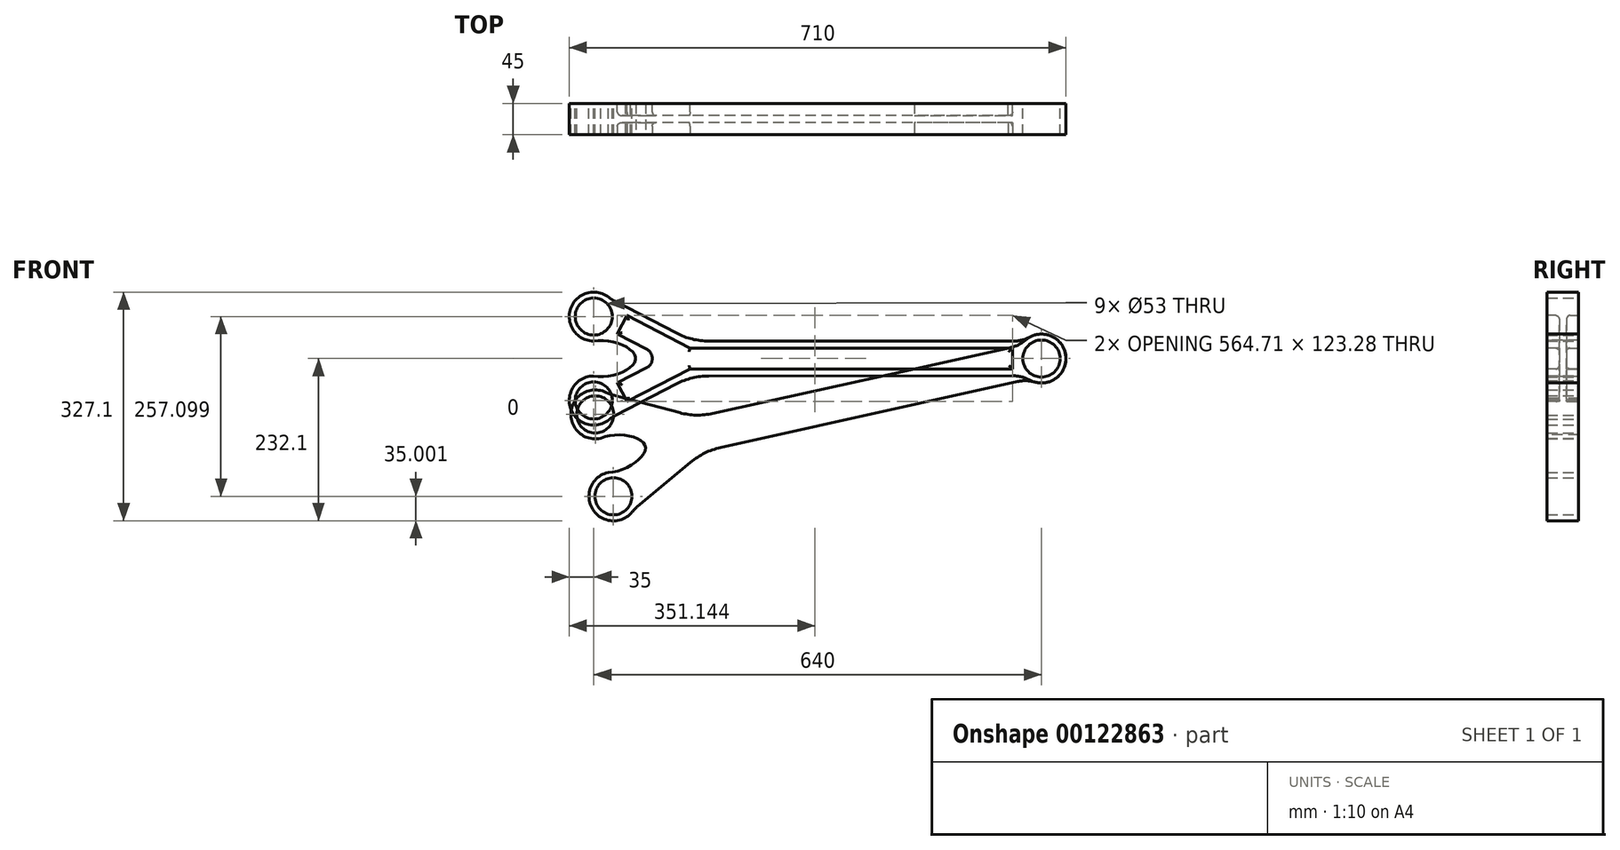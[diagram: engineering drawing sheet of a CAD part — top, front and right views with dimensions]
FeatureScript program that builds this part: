
annotation { "Feature Type Name" : "Feature", "Feature Type Description" : "" }
export const myFeature = defineFeature(function(context is Context, id is Id, definition is map)
    precondition{}
    {
        {
            var Q0;
            Q0=qCreatedBy(makeId("Front.planeOp"),FACE);
            var sketch = newSketch(context, id + "F0", { "sketchPlane" : qUnion([Q0])});
            skArc(sketch, "E0", {"start": v(-16.66, -30.78) * mm, "mid": v(35, 0) * mm, "end": v(-16.66, 30.78) * mm});
            skArc(sketch, "E1", {"start": v(-618.13, 87.33) * mm, "mid": v(-673.03, 71.59) * mm, "end": v(-640, 25) * mm});
            skCircle(sketch, "E2", {"center": v(-700, 0) * mm, "radius": 27.5 * mm, "construction": true});
            skCircle(sketch, "E3", {"center": v(-640, 60) * mm, "radius": 26.5 * mm});
            skCircle(sketch, "E4", {"center": v(-640, -60) * mm, "radius": 26.5 * mm});
            skCircle(sketch, "E5", {"center": v(0, 0) * mm, "radius": 26.5 * mm});
            skLineSegment(sketch, "E6", {"start": v(-40.48, 24.76) * mm, "end": v(-475.65, 24.99) * mm});
            skLineSegment(sketch, "E7", {"start": v(-40.48, -24.76) * mm, "end": v(-475.65, -24.99) * mm});
            skLineSegment(sketch, "E8", {"start": v(-521.62, -36.2) * mm, "end": v(-609.9, -81.98) * mm});
            skLineSegment(sketch, "E9", {"start": v(-521.62, 36.2) * mm, "end": v(-609.9, 81.98) * mm});
            skPoint(sketch, "E10.visualSharp", {"position": v(-500, 25) * mm});
            skArc(sketch, "E10.filletArc", {"start": v(-521.62, 36.2) * mm, "mid": v(-499.3, 27.84) * mm, "end": v(-475.65, 24.99) * mm});
            skPoint(sketch, "E11.visualSharp", {"position": v(-500, -25) * mm});
            skArc(sketch, "E11.filletArc", {"start": v(-475.65, -24.99) * mm, "mid": v(-499.3, -27.84) * mm, "end": v(-521.62, -36.2) * mm});
            skPoint(sketch, "E12.visualSharp", {"position": v(-615.25, 84.75) * mm});
            skArc(sketch, "E13", {"start": v(-640, -25) * mm, "mid": v(-673.03, -71.59) * mm, "end": v(-618.13, -87.33) * mm});
            skFitSpline(sketch, "E14", {"points": [v(-640, -25) * mm, v(-580, 0) * mm, v(-640, 25) * mm], "startDerivative": vector(150, -30) * mm, "endDerivative": vector(-150, -30) * mm});
            skPoint(sketch, "E15.visualSharp", {"position": v(-615.25, -84.75) * mm});
            skLineSegment(sketch, "E16", {"start": v(-24.75, 24.75) * mm, "end": v(0, 0) * mm, "construction": true});
            skLineSegment(sketch, "E17", {"start": v(-24.75, -24.75) * mm, "end": v(0, 0) * mm, "construction": true});
            skPoint(sketch, "E18.visualSharp", {"position": v(-24.75, 24.75) * mm});
            skArc(sketch, "E18.filletArc", {"start": v(-40.48, 24.76) * mm, "mid": v(-28.2, 26.28) * mm, "end": v(-16.66, 30.78) * mm});
            skPoint(sketch, "E19.visualSharp", {"position": v(-24.75, -24.75) * mm});
            skArc(sketch, "E19.filletArc", {"start": v(-16.66, -30.78) * mm, "mid": v(-28.2, -26.28) * mm, "end": v(-40.48, -24.76) * mm});
            skLineSegment(sketch, "E20", {"start": v(-615.25, 84.75) * mm, "end": v(-640, 60) * mm, "construction": true});
            skLineSegment(sketch, "E21", {"start": v(-640, -60) * mm, "end": v(-640, 177.49) * mm, "construction": true});
            skArc(sketch, "E22.filletArc", {"start": v(-618.13, 87.33) * mm, "mid": v(-614.15, 84.45) * mm, "end": v(-609.9, 81.98) * mm});
            skLineSegment(sketch, "E23", {"start": v(-615.25, -84.75) * mm, "end": v(-640, -60) * mm, "construction": true});
            skArc(sketch, "E24.filletArc", {"start": v(-609.9, -81.98) * mm, "mid": v(-614.15, -84.45) * mm, "end": v(-618.13, -87.33) * mm});
            skSolve(sketch);
        }
        {
            var Q0;
            Q0=qSketchRegion(id+"F0",true);
            extrude(context, id + "F1", {"entities" : qUnion([Q0]), "depth" : 45 * mm});
        }
        {
            var Q0;
            Q0=makeQuery(id+"F1.opExtrude","SWEPT_BODY",BODY,{"disambiguationData":[OSD([sQuery(id+"F0.wireOp",EDGE,"E0"),sQuery(id+"F0.wireOp",EDGE,"E1"),sQuery(id+"F0.wireOp",EDGE,"hKVllitM-rUlu-PjKN-B9u5-COeOs3Kio4uB"),sQuery(id+"F0.wireOp",EDGE,"bIEpRebq-8nbQ-7rQF-Jdrm-i3E8cfRsBNN9"),sQuery(id+"F0.wireOp",EDGE,"ymSRshFr-buK2-GFJu-27zL-H9ECYoIg19t0"),sQuery(id+"F0.wireOp",EDGE,"e6450e41-44a2-4cb5-af14-4686bec827bc"),sQuery(id+"F0.wireOp",EDGE,"ipdW7DlG-pZfv-p4Vr-qYAQ-uRQYnpMPVyQN"),sQuery(id+"F0.wireOp",EDGE,"9qNpO7d9-6r7V-397W-DIXA-CVevZtzhY8f4"),sQuery(id+"F0.wireOp",EDGE,"E3"),sQuery(id+"F0.wireOp",EDGE,"E4"),sQuery(id+"F0.wireOp",EDGE,"E5")])]});
            var Q1;
            Q1=makeQuery(id+"F1.opExtrude","CAP_EDGE",EDGE,{"disambiguationData":[OSD([sQuery(id+"F0.wireOp",EDGE,"E5")])],"isStart":false});
            transform(context, id + "F2", {"entities" : qUnion([Q0]), "transformType" : TransformType.ROTATION, "transformAxis" : qUnion([Q1]), "angle" : 12.5 * degree, "makeCopy" : true});
        }
        {
            var Q0;
            Q0=makeQuery(id+"F1.opExtrude","CAP_FACE",FACE,{"disambiguationData":[OSD([sQuery(id+"F0.wireOp",EDGE,"E0"),sQuery(id+"F0.wireOp",EDGE,"E1"),sQuery(id+"F0.wireOp",EDGE,"E3"),sQuery(id+"F0.wireOp",EDGE,"E4"),sQuery(id+"F0.wireOp",EDGE,"E5"),sQuery(id+"F0.wireOp",EDGE,"E6"),sQuery(id+"F0.wireOp",EDGE,"E7"),sQuery(id+"F0.wireOp",EDGE,"E8"),sQuery(id+"F0.wireOp",EDGE,"E9"),sQuery(id+"F0.wireOp",EDGE,"E10.filletArc"),sQuery(id+"F0.wireOp",EDGE,"E11.filletArc"),sQuery(id+"F0.wireOp",EDGE,"E13"),sQuery(id+"F0.wireOp",EDGE,"E14"),sQuery(id+"F0.wireOp",EDGE,"E18.filletArc"),sQuery(id+"F0.wireOp",EDGE,"E19.filletArc"),sQuery(id+"F0.wireOp",EDGE,"E22.filletArc"),sQuery(id+"F0.wireOp",EDGE,"E24.filletArc")])],"isStart":false});
            var sketch = newSketch(context, id + "F3", { "sketchPlane" : qUnion([Q0])});
            skLineSegment(sketch, "E25", {"start": v(-41.5, 14.76) * mm, "end": v(-502.44, 15) * mm});
            skLineSegment(sketch, "E26", {"start": v(-41.5, -14.76) * mm, "end": v(-502.44, -15) * mm});
            skLineSegment(sketch, "E27", {"start": v(-502.44, -15) * mm, "end": v(-592.4, -61.64) * mm});
            skLineSegment(sketch, "E28", {"start": v(-592.4, -61.64) * mm, "end": v(-606.21, -35) * mm});
            skLineSegment(sketch, "E29", {"start": v(-606.21, -35) * mm, "end": v(-564.37, -13.32) * mm});
            skLineSegment(sketch, "E30", {"start": v(-502.44, 15) * mm, "end": v(-592.4, 61.64) * mm});
            skLineSegment(sketch, "E31", {"start": v(-592.4, 61.64) * mm, "end": v(-606.21, 35) * mm});
            skLineSegment(sketch, "E32", {"start": v(-606.21, 35) * mm, "end": v(-564.37, 13.32) * mm});
            skPoint(sketch, "E33.visualSharp", {"position": v(-538.69, 0) * mm});
            skArc(sketch, "E33.filletArc", {"start": v(-564.37, -13.32) * mm, "mid": v(-556.28, 0) * mm, "end": v(-564.37, 13.32) * mm});
            skLineSegment(sketch, "E34", {"start": v(-41.5, 14.76) * mm, "end": v(-41.5, -14.76) * mm});
            skSolve(sketch);
        }
        {
            var Q0;
            Q0=qSketchRegion(id+"F3",true);
            extrude(context, id + "F4", {"entities" : qUnion([Q0]), "operationType" : NewBodyOperationType.REMOVE, "oppositeDirection" : true, "depth" : 17.5 * mm});
        }
        {
            var Q0;
            Q0=makeQuery(id+"F1.opExtrude","CAP_FACE",FACE,{"disambiguationData":[OSD([sQuery(id+"F0.wireOp",EDGE,"E0"),sQuery(id+"F0.wireOp",EDGE,"E1"),sQuery(id+"F0.wireOp",EDGE,"E3"),sQuery(id+"F0.wireOp",EDGE,"E4"),sQuery(id+"F0.wireOp",EDGE,"E5"),sQuery(id+"F0.wireOp",EDGE,"E6"),sQuery(id+"F0.wireOp",EDGE,"E7"),sQuery(id+"F0.wireOp",EDGE,"E8"),sQuery(id+"F0.wireOp",EDGE,"E9"),sQuery(id+"F0.wireOp",EDGE,"E10.filletArc"),sQuery(id+"F0.wireOp",EDGE,"E11.filletArc"),sQuery(id+"F0.wireOp",EDGE,"E13"),sQuery(id+"F0.wireOp",EDGE,"E14"),sQuery(id+"F0.wireOp",EDGE,"E18.filletArc"),sQuery(id+"F0.wireOp",EDGE,"E19.filletArc"),sQuery(id+"F0.wireOp",EDGE,"E22.filletArc"),sQuery(id+"F0.wireOp",EDGE,"E24.filletArc")])],"isStart":true});
            var sketch = newSketch(context, id + "F5", { "sketchPlane" : qUnion([Q0])});
            skLineSegment(sketch, "E35", {"start": v(41.5, 14.76) * mm, "end": v(502.44, 15) * mm});
            skLineSegment(sketch, "E36", {"start": v(502.44, 15) * mm, "end": v(592.4, 61.64) * mm});
            skLineSegment(sketch, "E37", {"start": v(592.4, 61.64) * mm, "end": v(606.21, 35) * mm});
            skLineSegment(sketch, "E38", {"start": v(606.21, -35) * mm, "end": v(592.4, -61.64) * mm});
            skLineSegment(sketch, "E39", {"start": v(592.4, -61.64) * mm, "end": v(502.44, -15) * mm});
            skLineSegment(sketch, "E40", {"start": v(502.44, -15) * mm, "end": v(41.5, -14.76) * mm});
            skLineSegment(sketch, "E41", {"start": v(41.5, 14.76) * mm, "end": v(41.5, -14.76) * mm});
            skLineSegment(sketch, "E42", {"start": v(606.21, 35) * mm, "end": v(564.37, 13.32) * mm});
            skLineSegment(sketch, "E43", {"start": v(564.37, -13.32) * mm, "end": v(606.21, -35) * mm});
            skPoint(sketch, "E44.visualSharp", {"position": v(538.69, 0) * mm});
            skArc(sketch, "E44.filletArc", {"start": v(564.37, 13.32) * mm, "mid": v(556.28, 0) * mm, "end": v(564.37, -13.32) * mm});
            skSolve(sketch);
        }
        {
            var Q0;
            Q0=qSketchRegion(id+"F5",true);
            extrude(context, id + "F6", {"entities" : qUnion([Q0]), "operationType" : NewBodyOperationType.REMOVE, "oppositeDirection" : true, "depth" : 17.5 * mm});
        }
        {
            var Q0;
            Q0=makeQuery(id+"F6.boolean.opBoolean","COPY",EDGE,{"derivedFrom":makeQuery(id+"F6.opExtrude","CAP_EDGE",EDGE,{"disambiguationData":[OSD([sQuery(id+"F5.wireOp",EDGE,"E35")])],"isStart":false})});
            var Q1;
            Q1=makeQuery(id+"F6.boolean.opBoolean","COPY",EDGE,{"derivedFrom":makeQuery(id+"F6.opExtrude","CAP_EDGE",EDGE,{"disambiguationData":[OSD([sQuery(id+"F5.wireOp",EDGE,"E41")])],"isStart":false})});
            var Q2;
            Q2=makeQuery(id+"F6.boolean.opBoolean","COPY",EDGE,{"derivedFrom":makeQuery(id+"F6.opExtrude","CAP_EDGE",EDGE,{"disambiguationData":[OSD([sQuery(id+"F5.wireOp",EDGE,"E40")])],"isStart":false})});
            var Q3;
            Q3=makeQuery(id+"F6.boolean.opBoolean","COPY",EDGE,{"derivedFrom":makeQuery(id+"F6.opExtrude","CAP_EDGE",EDGE,{"disambiguationData":[OSD([sQuery(id+"F5.wireOp",EDGE,"E36")])],"isStart":false})});
            var Q4;
            Q4=makeQuery(id+"F6.boolean.opBoolean","COPY",EDGE,{"derivedFrom":makeQuery(id+"F6.opExtrude","CAP_EDGE",EDGE,{"disambiguationData":[OSD([sQuery(id+"F5.wireOp",EDGE,"E39")])],"isStart":false})});
            var Q5;
            Q5=makeQuery(id+"F6.boolean.opBoolean","COPY",EDGE,{"derivedFrom":makeQuery(id+"F6.opExtrude","CAP_EDGE",EDGE,{"disambiguationData":[OSD([sQuery(id+"F5.wireOp",EDGE,"E38")])],"isStart":false})});
            var Q6;
            Q6=makeQuery(id+"F6.boolean.opBoolean","COPY",EDGE,{"derivedFrom":makeQuery(id+"F6.opExtrude","CAP_EDGE",EDGE,{"disambiguationData":[OSD([sQuery(id+"F5.wireOp",EDGE,"E43")])],"isStart":false})});
            var Q7;
            Q7=makeQuery(id+"F6.boolean.opBoolean","COPY",EDGE,{"derivedFrom":makeQuery(id+"F6.opExtrude","CAP_EDGE",EDGE,{"disambiguationData":[OSD([sQuery(id+"F5.wireOp",EDGE,"E37")])],"isStart":false})});
            fillet(context, id + "F7", {"entities" : qUnion([Q0, Q1, Q2, Q3, Q4, Q5, Q6, Q7]), "radius" : 5 * mm, "tangentPropagation" : true, "allowEdgeOverflow" : false});
        }
        {
            var Q0;
            Q0=makeQuery(id+"F4.boolean.opBoolean","COPY",EDGE,{"derivedFrom":makeQuery(id+"F4.opExtrude","CAP_EDGE",EDGE,{"disambiguationData":[OSD([sQuery(id+"F3.wireOp",EDGE,"E28")])],"isStart":false})});
            var Q1;
            Q1=makeQuery(id+"F4.boolean.opBoolean","COPY",EDGE,{"derivedFrom":makeQuery(id+"F4.opExtrude","CAP_EDGE",EDGE,{"disambiguationData":[OSD([sQuery(id+"F3.wireOp",EDGE,"E27")])],"isStart":false})});
            var Q2;
            Q2=makeQuery(id+"F4.boolean.opBoolean","COPY",EDGE,{"derivedFrom":makeQuery(id+"F4.opExtrude","CAP_EDGE",EDGE,{"disambiguationData":[OSD([sQuery(id+"F3.wireOp",EDGE,"E26")])],"isStart":false})});
            var Q3;
            Q3=makeQuery(id+"F4.boolean.opBoolean","COPY",EDGE,{"derivedFrom":makeQuery(id+"F4.opExtrude","CAP_EDGE",EDGE,{"disambiguationData":[OSD([sQuery(id+"F3.wireOp",EDGE,"E32")])],"isStart":false})});
            var Q4;
            Q4=makeQuery(id+"F4.boolean.opBoolean","COPY",EDGE,{"derivedFrom":makeQuery(id+"F4.opExtrude","CAP_EDGE",EDGE,{"disambiguationData":[OSD([sQuery(id+"F3.wireOp",EDGE,"E31")])],"isStart":false})});
            var Q5;
            Q5=makeQuery(id+"F4.boolean.opBoolean","COPY",EDGE,{"derivedFrom":makeQuery(id+"F4.opExtrude","CAP_EDGE",EDGE,{"disambiguationData":[OSD([sQuery(id+"F3.wireOp",EDGE,"E30")])],"isStart":false})});
            var Q6;
            Q6=makeQuery(id+"F4.boolean.opBoolean","COPY",EDGE,{"derivedFrom":makeQuery(id+"F4.opExtrude","CAP_EDGE",EDGE,{"disambiguationData":[OSD([sQuery(id+"F3.wireOp",EDGE,"E25")])],"isStart":false})});
            var Q7;
            Q7=makeQuery(id+"F4.boolean.opBoolean","COPY",EDGE,{"derivedFrom":makeQuery(id+"F4.opExtrude","CAP_EDGE",EDGE,{"disambiguationData":[OSD([sQuery(id+"F3.wireOp",EDGE,"E34")])],"isStart":false})});
            fillet(context, id + "F8", {"entities" : qUnion([Q0, Q1, Q2, Q3, Q4, Q5, Q6, Q7]), "radius" : 5 * mm, "tangentPropagation" : true, "allowEdgeOverflow" : false});
        }
        {
            var Q0;
            Q0=makeQuery(id+"F1.opExtrude","SWEPT_BODY",BODY,{"disambiguationData":[OSD([sQuery(id+"F0.wireOp",EDGE,"E0"),sQuery(id+"F0.wireOp",EDGE,"E1"),sQuery(id+"F0.wireOp",EDGE,"E3"),sQuery(id+"F0.wireOp",EDGE,"E4"),sQuery(id+"F0.wireOp",EDGE,"E5"),sQuery(id+"F0.wireOp",EDGE,"E6"),sQuery(id+"F0.wireOp",EDGE,"E7"),sQuery(id+"F0.wireOp",EDGE,"E8"),sQuery(id+"F0.wireOp",EDGE,"E9"),sQuery(id+"F0.wireOp",EDGE,"E10.filletArc"),sQuery(id+"F0.wireOp",EDGE,"E11.filletArc"),sQuery(id+"F0.wireOp",EDGE,"E13"),sQuery(id+"F0.wireOp",EDGE,"E14"),sQuery(id+"F0.wireOp",EDGE,"E18.filletArc"),sQuery(id+"F0.wireOp",EDGE,"E19.filletArc"),sQuery(id+"F0.wireOp",EDGE,"E22.filletArc"),sQuery(id+"F0.wireOp",EDGE,"E24.filletArc")])]});
            transform(context, id + "F9", {"entities" : qUnion([Q0]), "transformType" : TransformType.TRANSLATION_3D, "dx" : 0 * mm, "dy" : 0 * mm, "dz" : 0 * mm, "makeCopy" : true});
        }
    });
